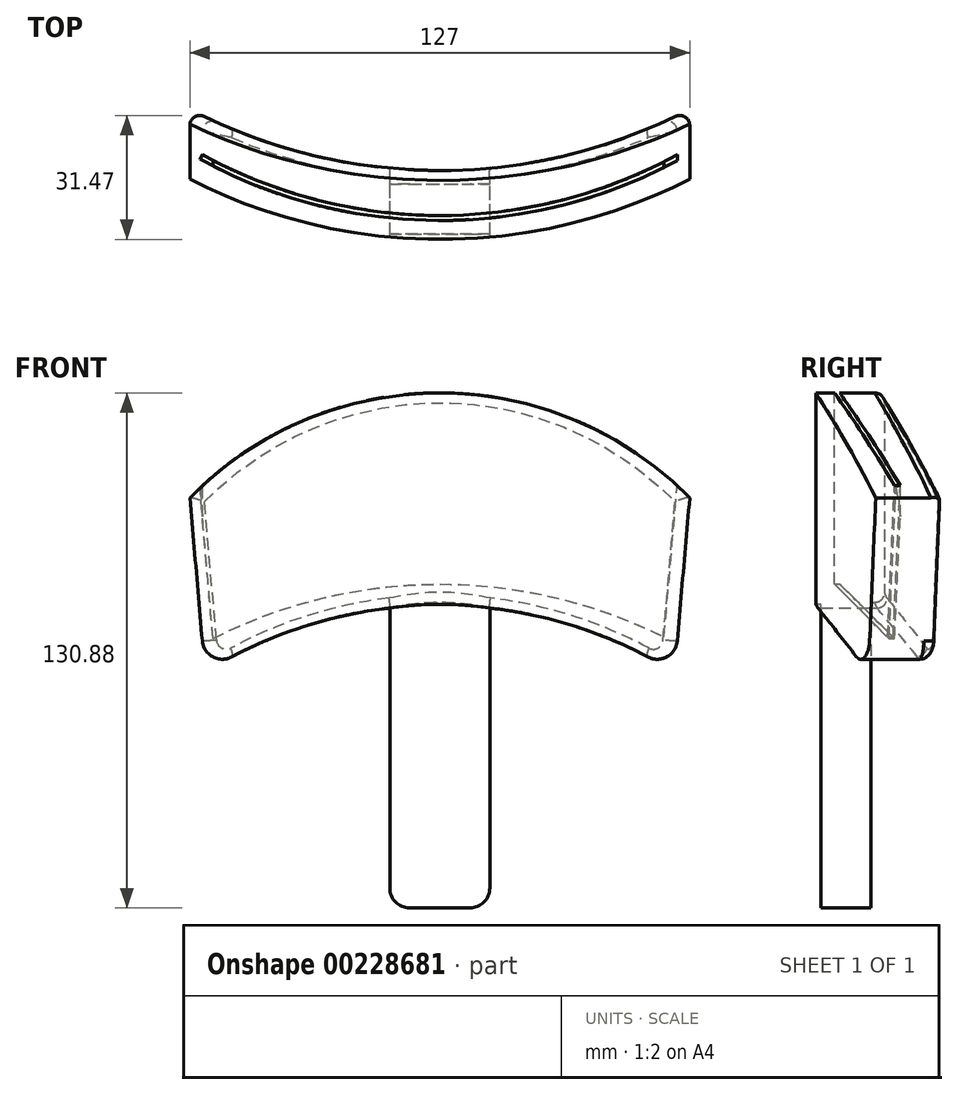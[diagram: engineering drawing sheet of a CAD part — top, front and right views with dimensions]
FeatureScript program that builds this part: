
annotation { "Feature Type Name" : "Feature", "Feature Type Description" : "" }
export const myFeature = defineFeature(function(context is Context, id is Id, definition is map)
    precondition{}
    {
        {
            var Q0;
            Q0=qCreatedBy(makeId("Front.planeOp"),FACE);
            var sketch = newSketch(context, id + "F0", { "sketchPlane" : qUnion([Q0])});
            skArc(sketch, "E0", {"start": v(63.5, 0) * mm, "mid": v(0, 26.68) * mm, "end": v(-63.5, 0) * mm});
            skLineSegment(sketch, "E1", {"start": v(-63.5, 0) * mm, "end": v(0, 0) * mm, "construction": true});
            skLineSegment(sketch, "E2", {"start": v(0, 0) * mm, "end": v(63.5, 0) * mm, "construction": true});
            skLineSegment(sketch, "E3", {"start": v(-63.5, 0) * mm, "end": v(-59.63, -44.28) * mm});
            skLineSegment(sketch, "E4", {"start": v(63.5, 0) * mm, "end": v(59.63, -44.28) * mm});
            skArc(sketch, "E5", {"start": v(59.63, -44.28) * mm, "mid": v(0, -27.28) * mm, "end": v(-59.63, -44.28) * mm});
            skLineSegment(sketch, "E6.bottom", {"start": v(-12.7, -28) * mm, "end": v(12.7, -28) * mm});
            skLineSegment(sketch, "E6.top", {"start": v(-12.7, -104.2) * mm, "end": v(12.7, -104.2) * mm});
            skLineSegment(sketch, "E6.left", {"start": v(-12.7, -28) * mm, "end": v(-12.7, -104.2) * mm});
            skLineSegment(sketch, "E6.right", {"start": v(12.7, -28) * mm, "end": v(12.7, -104.2) * mm});
            skSolve(sketch);
        }
        {
            var Q0;
            Q0=qSketchRegion(id+"F0",true);
            extrude(context, id + "F1", {"entities" : qUnion([Q0]), "depth" : 44.45 * mm});
        }
        {
            var Q0;
            Q0=makeQuery(id+"F1.opExtrude","CAP_FACE",FACE,{"disambiguationData":[OSD([sQuery(id+"F0.wireOp",EDGE,"E0"),sQuery(id+"F0.wireOp",EDGE,"E3"),sQuery(id+"F0.wireOp",EDGE,"E4"),sQuery(id+"F0.wireOp",EDGE,"E5"),sQuery(id+"F0.wireOp",EDGE,"E6.top"),sQuery(id+"F0.wireOp",EDGE,"E6.left"),sQuery(id+"F0.wireOp",EDGE,"E6.right")])],"isStart":false});
            var sketch = newSketch(context, id + "F2", { "sketchPlane" : qUnion([Q0])});
            skArc(sketch, "E7", {"start": v(12.7, -28) * mm, "mid": v(0, -27.05) * mm, "end": v(-12.7, -28) * mm});
            skLineSegment(sketch, "E8", {"start": v(-12.7, -28) * mm, "end": v(-12.7, -104.2) * mm});
            skLineSegment(sketch, "E9", {"start": v(-12.7, -104.2) * mm, "end": v(12.7, -104.2) * mm});
            skLineSegment(sketch, "E10", {"start": v(12.7, -104.2) * mm, "end": v(12.7, -28) * mm});
            skSolve(sketch);
        }
        {
            var Q0;
            Q0=qSketchRegion(id+"F2",true);
            extrude(context, id + "F3", {"entities" : qUnion([Q0]), "operationType" : NewBodyOperationType.REMOVE, "oppositeDirection" : true, "depth" : 6.35 * mm});
        }
        {
            var Q0;
            Q0=makeQuery(id+"F1.opExtrude","CAP_FACE",FACE,{"disambiguationData":[OSD([sQuery(id+"F0.wireOp",EDGE,"E0"),sQuery(id+"F0.wireOp",EDGE,"E3"),sQuery(id+"F0.wireOp",EDGE,"E4"),sQuery(id+"F0.wireOp",EDGE,"E5"),sQuery(id+"F0.wireOp",EDGE,"E6.top"),sQuery(id+"F0.wireOp",EDGE,"E6.left"),sQuery(id+"F0.wireOp",EDGE,"E6.right")])],"isStart":true});
            var sketch = newSketch(context, id + "F4", { "sketchPlane" : qUnion([Q0])});
            skArc(sketch, "E11", {"start": v(12.7, -28) * mm, "mid": v(0, -26.56) * mm, "end": v(-12.7, -28) * mm});
            skLineSegment(sketch, "E12", {"start": v(-12.7, -28) * mm, "end": v(-12.7, -104.2) * mm});
            skLineSegment(sketch, "E13", {"start": v(-12.7, -104.2) * mm, "end": v(12.7, -104.2) * mm});
            skLineSegment(sketch, "E14", {"start": v(12.7, -104.2) * mm, "end": v(12.7, -28) * mm});
            skSolve(sketch);
        }
        {
            var Q0;
            Q0=qSketchRegion(id+"F4",true);
            extrude(context, id + "F5", {"entities" : qUnion([Q0]), "operationType" : NewBodyOperationType.REMOVE, "oppositeDirection" : true, "depth" : 25.4 * mm});
        }
        {
            var Q0;
            Q0=makeQuery(id+"F1.opExtrude","SWEPT_FACE",FACE,{"disambiguationData":[OSD([sQuery(id+"F0.wireOp",EDGE,"E6.top")])]});
            var sketch = newSketch(context, id + "F6", { "sketchPlane" : qUnion([Q0])});
            skArc(sketch, "E15", {"start": v(-63.5, 6.35) * mm, "mid": v(0, 21.92) * mm, "end": v(63.5, 6.35) * mm});
            skLineSegment(sketch, "E16", {"start": v(-63.5, 6.35) * mm, "end": v(-63.5, 0) * mm});
            skLineSegment(sketch, "E17", {"start": v(-63.5, 0) * mm, "end": v(63.5, 0) * mm});
            skLineSegment(sketch, "E18", {"start": v(63.5, 0) * mm, "end": v(63.5, 6.35) * mm});
            skSolve(sketch);
        }
        {
            var Q0;
            Q0=makeQuery(id+"F1.opExtrude","SWEPT_FACE",FACE,{"disambiguationData":[OSD([sQuery(id+"F0.wireOp",EDGE,"E6.top")])]});
            var sketch = newSketch(context, id + "F7", { "sketchPlane" : qUnion([Q0])});
            skArc(sketch, "E19", {"start": v(63.5, 24.16) * mm, "mid": v(0, 39.43) * mm, "end": v(-63.5, 24.16) * mm});
            skLineSegment(sketch, "E20", {"start": v(-63.5, 24.16) * mm, "end": v(-63.5, 50.78) * mm});
            skLineSegment(sketch, "E21", {"start": v(-63.5, 50.78) * mm, "end": v(63.78, 50.78) * mm});
            skLineSegment(sketch, "E22", {"start": v(63.78, 50.78) * mm, "end": v(63.5, 24.16) * mm});
            skSolve(sketch);
        }
        {
            var Q0;
            Q0=makeQuery(id+"F1.opExtrude","SWEPT_FACE",FACE,{"disambiguationData":[OSD([sQuery(id+"F0.wireOp",EDGE,"E6.top")])]});
            cPlane(context, id + "F8", {"entities" : qUnion([Q0]), "cplaneType" : CPlaneType.OFFSET, "offset" : 132.08 * mm, "oppositeDirection" : true, "width" : 152.4 * mm, "height" : 152.4 * mm});
        }
        {
            var Q0;
            Q0=qCreatedBy(id+"F8.planeOp",FACE);
            var sketch = newSketch(context, id + "F9", { "sketchPlane" : qUnion([Q0])});
            skArc(sketch, "E23", {"start": v(60.96, 19.05) * mm, "mid": v(0, 34.64) * mm, "end": v(-60.96, 19.05) * mm});
            skLineSegment(sketch, "E24", {"start": v(-63.5, 19.05) * mm, "end": v(-60.96, 19.05) * mm, "construction": true});
            skLineSegment(sketch, "E25", {"start": v(0, 0) * mm, "end": v(0, 53.93) * mm, "construction": true});
            skLineSegment(sketch, "E26.MirrorCS", {"start": v(63.5, 19.05) * mm, "end": v(60.96, 19.05) * mm, "construction": true});
            skLineSegment(sketch, "E27", {"start": v(-60.96, 19.05) * mm, "end": v(60.96, 19.05) * mm, "construction": true});
            skLineSegment(sketch, "E28", {"start": v(-60.96, 19.05) * mm, "end": v(-60.33, 17.95) * mm});
            skArc(sketch, "E29", {"start": v(0, 33.37) * mm, "mid": v(-31.12, 29.41) * mm, "end": v(-60.33, 17.95) * mm});
            skArc(sketch, "E30.MirrorCS", {"start": v(0, 33.37) * mm, "mid": v(31.12, 29.41) * mm, "end": v(60.33, 17.95) * mm});
            skLineSegment(sketch, "E31.MirrorCS", {"start": v(60.96, 19.05) * mm, "end": v(60.33, 17.95) * mm});
            skSolve(sketch);
        }
        {
            var Q0;
            Q0=qSketchRegion(id+"F9",true);
            extrude(context, id + "F10", {"entities" : qUnion([Q0]), "operationType" : NewBodyOperationType.REMOVE, "depth" : 69.85 * mm});
        }
        {
            var Q0;
            Q0=makeQuery(id+"F1.opExtrude","CAP_FACE",FACE,{"disambiguationData":[OSD([sQuery(id+"F0.wireOp",EDGE,"E0"),sQuery(id+"F0.wireOp",EDGE,"E3"),sQuery(id+"F0.wireOp",EDGE,"E4"),sQuery(id+"F0.wireOp",EDGE,"E5"),sQuery(id+"F0.wireOp",EDGE,"E6.top"),sQuery(id+"F0.wireOp",EDGE,"E6.left"),sQuery(id+"F0.wireOp",EDGE,"E6.right")])],"isStart":true});
            var sketch = newSketch(context, id + "F11", { "sketchPlane" : qUnion([Q0])});
            skArc(sketch, "E32", {"start": v(57.61, -35.75) * mm, "mid": v(0.37, -21.91) * mm, "end": v(-56.96, -35.4) * mm});
            skLineSegment(sketch, "E33", {"start": v(-56.96, -35.4) * mm, "end": v(-60.33, 3.08) * mm});
            skLineSegment(sketch, "E34", {"start": v(57.61, -35.75) * mm, "end": v(60.96, 2.5) * mm});
            skArc(sketch, "E35", {"start": v(-60.33, 3.08) * mm, "mid": v(-61.93, 1.56) * mm, "end": v(-63.5, 0) * mm});
            skLineSegment(sketch, "E36", {"start": v(-63.5, 0) * mm, "end": v(-59.63, -44.28) * mm});
            skArc(sketch, "E37", {"start": v(-12.7, -28) * mm, "mid": v(-37.07, -33.53) * mm, "end": v(-59.63, -44.28) * mm});
            skArc(sketch, "E38", {"start": v(0, -26.56) * mm, "mid": v(-6.4, -26.92) * mm, "end": v(-12.7, -28) * mm});
            skLineSegment(sketch, "E39", {"start": v(0, 0) * mm, "end": v(0, 17.87) * mm, "construction": true});
            skArc(sketch, "E40.MirrorCS", {"start": v(0, -26.56) * mm, "mid": v(6.4, -26.92) * mm, "end": v(12.7, -28) * mm});
            skArc(sketch, "E41.MirrorCS", {"start": v(12.7, -28) * mm, "mid": v(37.07, -33.53) * mm, "end": v(59.63, -44.28) * mm});
            skLineSegment(sketch, "E42.MirrorCS", {"start": v(63.5, 0) * mm, "end": v(59.63, -44.28) * mm});
            skArc(sketch, "E43.MirrorCS", {"start": v(60.33, 3.08) * mm, "mid": v(61.93, 1.56) * mm, "end": v(63.5, 0) * mm});
            skSolve(sketch);
        }
        {
            var Q0;
            Q0=qSketchRegion(id+"F11",true);
            extrude(context, id + "F12", {"entities" : qUnion([Q0]), "operationType" : NewBodyOperationType.ADD, "oppositeDirection" : true, "depth" : 44.45 * mm});
        }
        {
            var Q0;
            Q0=qSketchRegion(id+"F6",true);
            extrude(context, id + "F13", {"entities" : qUnion([Q0]), "operationType" : NewBodyOperationType.REMOVE, "endBound" : BoundingType.THROUGH_ALL, "oppositeDirection" : true, "depth" : 25.4 * mm});
        }
        {
            var Q0;
            Q0=qSketchRegion(id+"F7",true);
            extrude(context, id + "F14", {"entities" : qUnion([Q0]), "operationType" : NewBodyOperationType.REMOVE, "endBound" : BoundingType.THROUGH_ALL, "oppositeDirection" : true, "depth" : 25.4 * mm});
        }
        {
            var Q0;
            Q0=makeQuery(id+"F3.boolean.opBoolean","COPY",FACE,{"derivedFrom":makeQuery(id+"F3.opExtrude","CAP_FACE",FACE,{"disambiguationData":[OSD([sQuery(id+"F2.wireOp",EDGE,"E7"),sQuery(id+"F2.wireOp",EDGE,"E8"),sQuery(id+"F2.wireOp",EDGE,"E9"),sQuery(id+"F2.wireOp",EDGE,"E10")])],"isStart":false})});
            var sketch = newSketch(context, id + "F15", { "sketchPlane" : qUnion([Q0])});
            skArc(sketch, "E44", {"start": v(12.7, -28) * mm, "mid": v(0, -27.05) * mm, "end": v(-12.7, -28) * mm});
            skLineSegment(sketch, "E45", {"start": v(-12.7, -28) * mm, "end": v(-12.7, -55.54) * mm});
            skLineSegment(sketch, "E46", {"start": v(-12.7, -55.54) * mm, "end": v(12.7, -55.54) * mm});
            skLineSegment(sketch, "E47", {"start": v(12.7, -55.54) * mm, "end": v(12.7, -28) * mm});
            skSolve(sketch);
        }
        {
            var Q0;
            Q0=makeQuery(id+"F5.boolean.opBoolean","COPY",FACE,{"derivedFrom":makeQuery(id+"F5.opExtrude","CAP_FACE",FACE,{"disambiguationData":[OSD([sQuery(id+"F4.wireOp",EDGE,"E11"),sQuery(id+"F4.wireOp",EDGE,"E12"),sQuery(id+"F4.wireOp",EDGE,"E13"),sQuery(id+"F4.wireOp",EDGE,"E14")])],"isStart":false})});
            var sketch = newSketch(context, id + "F16", { "sketchPlane" : qUnion([Q0])});
            skArc(sketch, "E48", {"start": v(12.7, -28) * mm, "mid": v(0, -26.56) * mm, "end": v(-12.7, -28) * mm});
            skLineSegment(sketch, "E49.bottom", {"start": v(-12.7, -28) * mm, "end": v(12.7, -28) * mm});
            skLineSegment(sketch, "E49.top", {"start": v(-12.7, -60.4) * mm, "end": v(12.7, -60.4) * mm});
            skLineSegment(sketch, "E49.left", {"start": v(-12.7, -28) * mm, "end": v(-12.7, -60.4) * mm});
            skLineSegment(sketch, "E49.right", {"start": v(12.7, -28) * mm, "end": v(12.7, -60.4) * mm});
            skSolve(sketch);
        }
        {
            var Q0;
            Q0=qSketchRegion(id+"F16",true);
            extrude(context, id + "F17", {"entities" : qUnion([Q0]), "operationType" : NewBodyOperationType.ADD, "oppositeDirection" : true, "depth" : 12.7 * mm});
        }
        {
            var Q0;
            Q0=makeQuery(id+"F13.boolean.opBoolean","COPY",FACE,{"derivedFrom":makeQuery(id+"F13.opExtrude","SWEPT_FACE",FACE,{"disambiguationData":[OSD([sQuery(id+"F6.wireOp",EDGE,"E15")])]})});
            fillet(context, id + "F18", {"entities" : qUnion([Q0]), "radius" : 2.54 * mm, "tangentPropagation" : true, "allowEdgeOverflow" : false});
        }
        {
            var Q0;
            Q0=makeQuery(id+"F5.boolean.opBoolean","COPY",EDGE,{"derivedFrom":makeQuery(id+"F5.opExtrude","CAP_EDGE",EDGE,{"disambiguationData":[OSD([sQuery(id+"F4.wireOp",EDGE,"E12")])],"isStart":false})});
            var Q1;
            Q1=makeQuery(id+"F3.boolean.opBoolean","COPY",EDGE,{"derivedFrom":makeQuery(id+"F3.opExtrude","CAP_EDGE",EDGE,{"disambiguationData":[OSD([sQuery(id+"F2.wireOp",EDGE,"E10")])],"isStart":false})});
            var Q2;
            Q2=makeQuery(id+"F3.boolean.opBoolean","COPY",EDGE,{"derivedFrom":makeQuery(id+"F3.opExtrude","CAP_EDGE",EDGE,{"disambiguationData":[OSD([sQuery(id+"F2.wireOp",EDGE,"E8")])],"isStart":false})});
            var Q3;
            Q3=makeQuery(id+"F5.boolean.opBoolean","COPY",EDGE,{"derivedFrom":makeQuery(id+"F5.opExtrude","CAP_EDGE",EDGE,{"disambiguationData":[OSD([sQuery(id+"F4.wireOp",EDGE,"E14")])],"isStart":false})});
            var Q4;
            Q4=makeQuery(id+"F5.boolean.opBoolean","COPY",EDGE,{"derivedFrom":makeQuery(id+"F5.opExtrude","CAP_EDGE",EDGE,{"disambiguationData":[OSD([sQuery(id+"F4.wireOp",EDGE,"E13")])],"isStart":false})});
            var Q5;
            Q5=makeQuery(id+"F1.opExtrude","SWEPT_EDGE",EDGE,{"disambiguationData":[OSD([sQuery(id+"F0.wireOp",EDGE,"E6.top"),sQuery(id+"F0.wireOp",EDGE,"E6.left")])]});
            var Q6;
            Q6=makeQuery(id+"F3.boolean.opBoolean","COPY",EDGE,{"derivedFrom":makeQuery(id+"F3.opExtrude","CAP_EDGE",EDGE,{"disambiguationData":[OSD([sQuery(id+"F2.wireOp",EDGE,"E9")])],"isStart":false})});
            var Q7;
            Q7=makeQuery(id+"F1.opExtrude","SWEPT_EDGE",EDGE,{"disambiguationData":[OSD([sQuery(id+"F0.wireOp",EDGE,"E6.top"),sQuery(id+"F0.wireOp",EDGE,"E6.right")])]});
            fillet(context, id + "F19", {"entities" : qUnion([Q0, Q1, Q2, Q3, Q4, Q5, Q6, Q7]), "radius" : 5.08 * mm, "tangentPropagation" : true, "allowEdgeOverflow" : false});
        }
        {
            var Q0;
            Q0=makeQuery(id+"F1.opExtrude","SWEPT_EDGE",EDGE,{"disambiguationData":[OSD([sQuery(id+"F0.wireOp",EDGE,"E3"),sQuery(id+"F0.wireOp",EDGE,"E5")])]});
            var Q1;
            Q1=makeQuery(id+"F1.opExtrude","SWEPT_EDGE",EDGE,{"disambiguationData":[OSD([sQuery(id+"F0.wireOp",EDGE,"E4"),sQuery(id+"F0.wireOp",EDGE,"E5")])]});
            fillet(context, id + "F20", {"entities" : qUnion([Q0, Q1]), "radius" : 5.08 * mm, "tangentPropagation" : true, "allowEdgeOverflow" : false});
        }
    });
